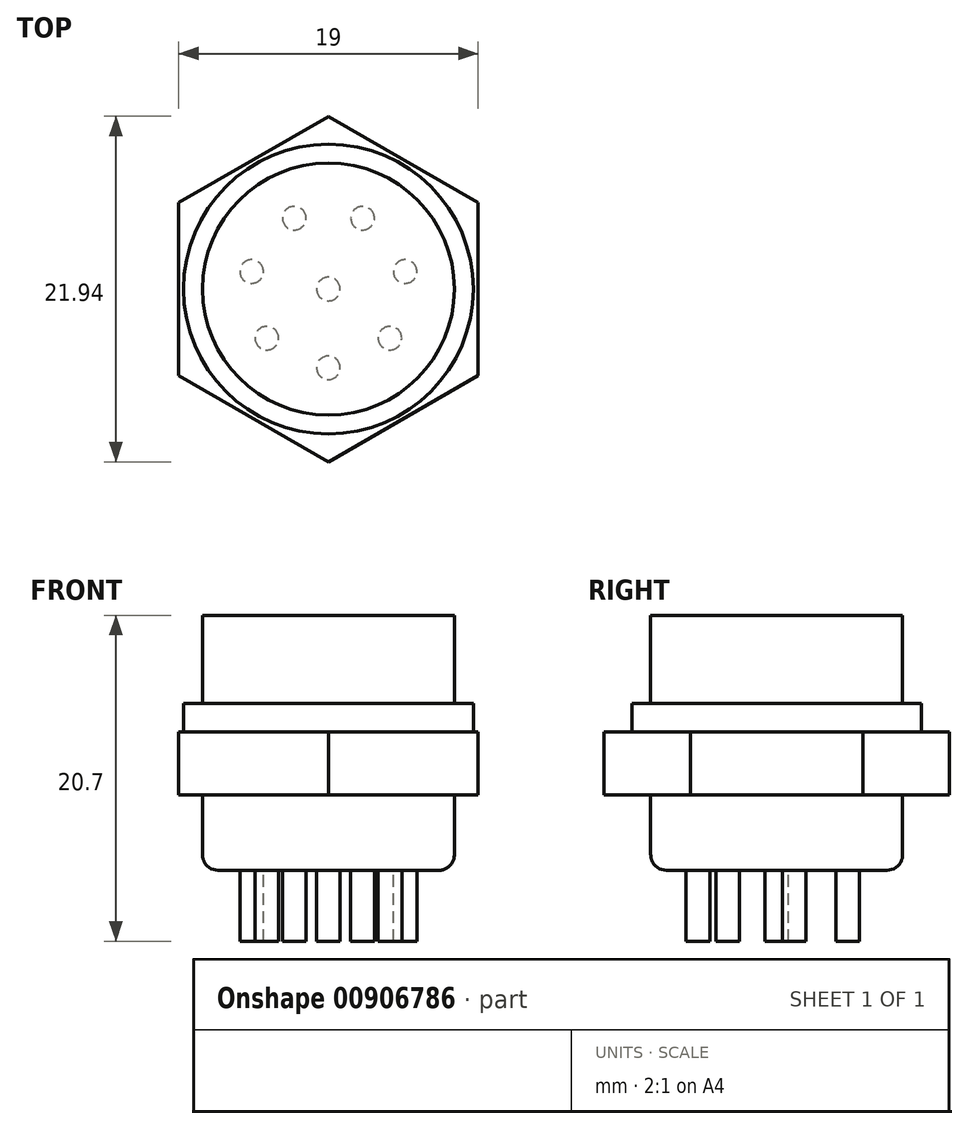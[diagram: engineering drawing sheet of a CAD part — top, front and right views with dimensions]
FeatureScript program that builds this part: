
annotation { "Feature Type Name" : "Feature", "Feature Type Description" : "" }
export const myFeature = defineFeature(function(context is Context, id is Id, definition is map)
    precondition{}
    {
        {
            var Q0;
            Q0=qCreatedBy(makeId("Front.planeOp"),FACE);
            var sketch = newSketch(context, id + "F0", { "sketchPlane" : qUnion([Q0])});
            skLineSegment(sketch, "E0", {"start": v(0, 0) * mm, "end": v(0, 16.2) * mm});
            skLineSegment(sketch, "E1", {"start": v(0, 16.2) * mm, "end": v(8, 16.2) * mm});
            skLineSegment(sketch, "E2", {"start": v(8, 16.2) * mm, "end": v(8, 10.6) * mm});
            skLineSegment(sketch, "E3", {"start": v(8, 10.6) * mm, "end": v(9.2, 10.6) * mm});
            skLineSegment(sketch, "E4", {"start": v(9.2, 10.6) * mm, "end": v(9.2, 8.8) * mm});
            skLineSegment(sketch, "E5", {"start": v(9.2, 8.8) * mm, "end": v(8, 8.8) * mm});
            skLineSegment(sketch, "E6", {"start": v(8, 8.8) * mm, "end": v(8, 0) * mm});
            skLineSegment(sketch, "E7", {"start": v(8, 0) * mm, "end": v(0, 0) * mm});
            skSolve(sketch);
        }
        {
            var Q0;
            Q0=makeQuery(id+"F0.imprint","IMPRINT",FACE,{"disambiguationData":[TD([[makeQuery(id+"F0.imprint","IMPRINT",EDGE,{"derivedFrom":sQuery(id+"F0.wireOp",EDGE,"E0")}),-1.0]])]});
            var Q1;
            Q1=sQuery(id+"F0.wireOp",EDGE,"E0");
            revolve(context, id + "F1", {"surfaceOperationType" : NewSurfaceOperationType.NEW, "entities" : qUnion([Q0]), "axis" : qUnion([Q1]), "revolveType" : RevolveType.FULL});
        }
        {
            var Q0;
            Q0=makeQuery(id+"F1.opRevolve","SWEPT_EDGE",EDGE,{"disambiguationData":[OSD([sQuery(id+"F0.wireOp",EDGE,"E6"),sQuery(id+"F0.wireOp",EDGE,"E7")])]});
            fillet(context, id + "F2", {"entities" : qUnion([Q0]), "radius" : 1 * mm, "tangentPropagation" : true, "allowEdgeOverflow" : false});
        }
        {
            var Q0;
            Q0=makeQuery(id+"F1.opRevolve","SWEPT_FACE",FACE,{"disambiguationData":[OSD([sQuery(id+"F0.wireOp",EDGE,"E7")])]});
            var sketch = newSketch(context, id + "F3", { "sketchPlane" : qUnion([Q0])});
            skCircle(sketch, "E8", {"center": v(0, 0) * mm, "radius": 0.75 * mm});
            skCircle(sketch, "E9", {"center": v(0, 5) * mm, "radius": 0.75 * mm});
            skCircle(sketch, "E10.1.0", {"center": v(-3.9, 3.12) * mm, "radius": 0.75 * mm});
            skCircle(sketch, "E10.2.0", {"center": v(-4.87, -1.11) * mm, "radius": 0.75 * mm});
            skCircle(sketch, "E10.3.0", {"center": v(-2.17, -4.5) * mm, "radius": 0.75 * mm});
            skCircle(sketch, "E10.4.0", {"center": v(2.17, -4.5) * mm, "radius": 0.75 * mm});
            skCircle(sketch, "E10.5.0", {"center": v(4.87, -1.11) * mm, "radius": 0.75 * mm});
            skCircle(sketch, "E10.6.0", {"center": v(3.9, 3.12) * mm, "radius": 0.75 * mm});
            skSolve(sketch);
        }
        {
            var Q0;
            Q0 = qSketchRegion(id + "F3", true);
            extrude(context, id + "F4", {"entities" : qUnion([Q0]), "operationType" : NewBodyOperationType.ADD, "depth" : 4.5 * mm, "offsetDistance" : 25 * mm});
        }
        {
            var Q0;
            Q0=makeQuery(id+"F1.opRevolve","SWEPT_FACE",FACE,{"disambiguationData":[OSD([sQuery(id+"F0.wireOp",EDGE,"E5")])]});
            var sketch = newSketch(context, id + "F5", { "sketchPlane" : qUnion([Q0])});
            skCircle(sketch, "E11.cCircle", {"center": v(0, 0) * mm, "radius": 9.5 * mm, "construction": true});
            skLineSegment(sketch, "E11.0", {"start": v(9.5, 5.48) * mm, "end": v(9.5, -5.48) * mm});
            skLineSegment(sketch, "E11.1", {"start": v(9.5, -5.48) * mm, "end": v(0, -10.97) * mm});
            skLineSegment(sketch, "E11.2", {"start": v(0, -10.97) * mm, "end": v(-9.5, -5.48) * mm});
            skLineSegment(sketch, "E11.3", {"start": v(-9.5, -5.48) * mm, "end": v(-9.5, 5.48) * mm});
            skLineSegment(sketch, "E11.4", {"start": v(-9.5, 5.48) * mm, "end": v(0, 10.97) * mm});
            skLineSegment(sketch, "E11.5", {"start": v(0, 10.97) * mm, "end": v(9.5, 5.48) * mm});
            skPoint(sketch, "E11.0.midPoint", {"position": v(9.5, 0) * mm});
            skSolve(sketch);
        }
        {
            var Q0;
            Q0=makeQuery(id+"F5.imprint","IMPRINT",FACE,{"disambiguationData":[TD([[makeQuery(id+"F5.imprint","IMPRINT",EDGE,{"derivedFrom":sQuery(id+"F5.wireOp",EDGE,"E11.0")}),-1.0]])]});
            var Q1;
            {var subQ0=sQuery(id+"F0.wireOp",EDGE,"E5");Q1=makeQuery(id+"F5.imprint","IMPRINT",FACE,{"disambiguationData":[TD([[makeQuery(id+"F5.imprint","IMPRINT",EDGE,{"derivedFrom":makeQuery(id+"F1.opRevolve","SWEPT_EDGE",EDGE,{"disambiguationData":[OSD([sQuery(id+"F0.wireOp",EDGE,"E4"),subQ0])]})}),1.0]])]});}
            extrude(context, id + "F6", {"entities" : qUnion([Q0, Q1]), "operationType" : NewBodyOperationType.ADD, "depth" : 4 * mm, "offsetDistance" : 25 * mm});
        }
    });
